# Revit family: Dock-Hood_Perma-Tech_Metal-Hood
name_source: partatom
category: Generic Models
units: mm (PartAtom-declared; Revit-internal decimal feet)

## family parameters
Always vertical = Yes
Can host rebar = No
Cut with Voids When Loaded = No
Maintain Annotation Orientation = No
Part Type = Normal
Room Calculation Point = No
Round Connector Dimension = Use Radius
Shared = No
Work Plane-Based = Yes

## types (2) — shared parameters
Arcat Spec = https://www.arcat.com
Default Elevation = 0' - 0"
Frame Space = 0' - 11 31/32"
Gusset Count = 3
Height = 0' - 6"
Hood = WHITE
Length = 4' - 0"
Manufacturer = Perma Tech Inc.
Product Documentation Link = https://www.permatechinc.com
Product Info = https://www.arcat.com
Product Page URL = https://www.permatechinc.com
Specification = https://www.permatechinc.com
Tabs Wire Count = 2
Taps Wire Space = 1' - 3 31/32"
URL = https://www.permatechinc.com
Width = 1' - 6"
X1 = 4
X2 = 3
zero-valued in all types: Cost

## per-type parameters (varying)
| type | Model | Tabs Wire |
| Metal Hoods | Perma Metal Hoods | No |
| Perma Metal Hood with Guide Wire | Perma Metal Hood with Guide Wire | Yes |

## geometry (parser evidence)
native form markers: Sweep x8
no freeform markers — native parametric forms only
